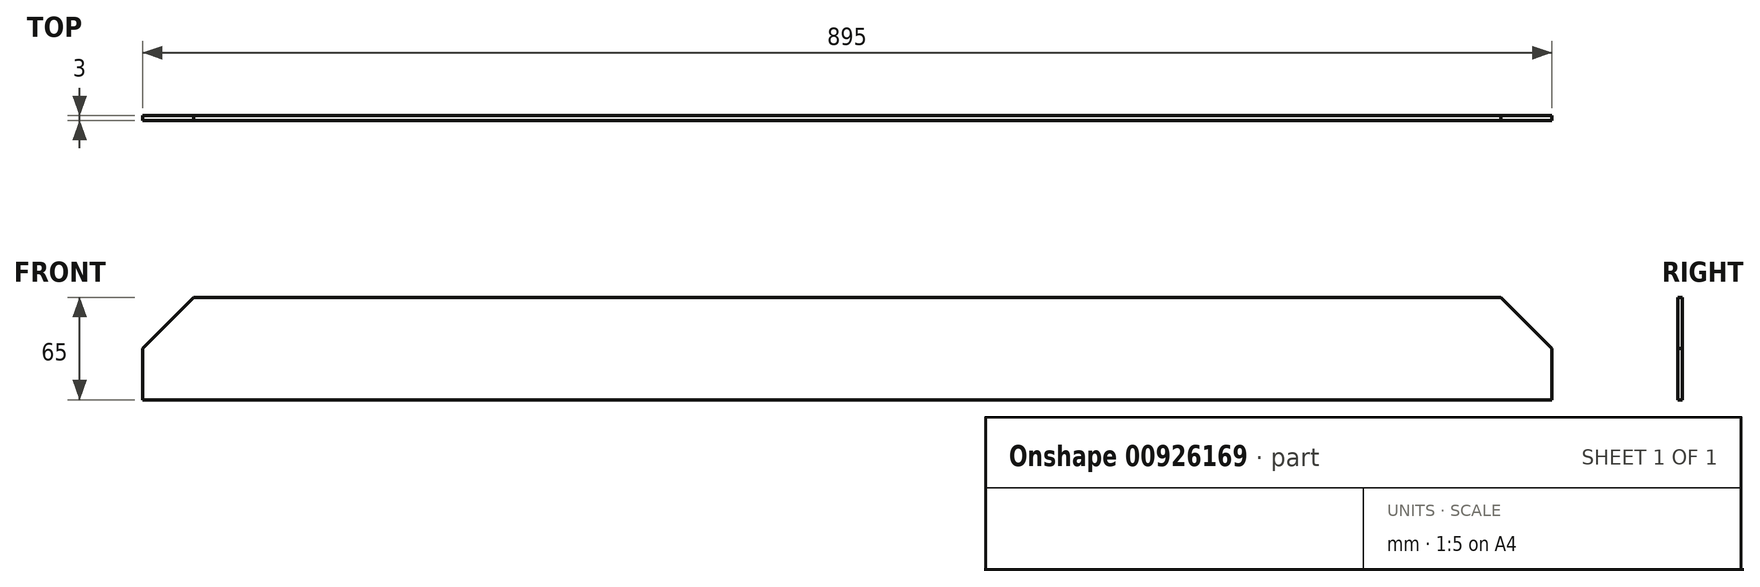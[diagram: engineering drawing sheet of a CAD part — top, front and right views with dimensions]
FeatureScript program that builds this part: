
annotation { "Feature Type Name" : "Feature", "Feature Type Description" : "" }
export const myFeature = defineFeature(function(context is Context, id is Id, definition is map)
    precondition{}
    {
        {
            var Q0;
            Q0=qCreatedBy(makeId("Top.planeOp"),FACE);
            var sketch = newSketch(context, id + "F0", { "sketchPlane" : qUnion([Q0])});
            skLineSegment(sketch, "E0.bottom", {"start": v(0, 0) * mm, "end": v(895, 0) * mm});
            skLineSegment(sketch, "E0.top", {"start": v(0, 3) * mm, "end": v(895, 3) * mm});
            skLineSegment(sketch, "E0.left", {"start": v(0, 0) * mm, "end": v(0, 3) * mm});
            skLineSegment(sketch, "E0.right", {"start": v(895, 0) * mm, "end": v(895, 3) * mm});
            skSolve(sketch);
        }
        {
            var Q0;
            Q0=makeQuery(id+"F0.imprint","IMPRINT",FACE,{"disambiguationData":[TD([[makeQuery(id+"F0.imprint","IMPRINT",EDGE,{"derivedFrom":sQuery(id+"F0.wireOp",EDGE,"E0.bottom")}),1.0]])]});
            extrude(context, id + "F1", {"entities" : qUnion([Q0]), "depth" : 65 * mm, "offsetDistance" : 25 * mm});
        }
        {
            var Q0;
            Q0=makeQuery(id+"F1.opExtrude","SWEPT_FACE",FACE,{"disambiguationData":[OSD([sQuery(id+"F0.wireOp",EDGE,"E0.bottom")])]});
            var sketch = newSketch(context, id + "F2", { "sketchPlane" : qUnion([Q0])});
            skLineSegment(sketch, "E1", {"start": v(0, 32.5) * mm, "end": v(32.5, 65) * mm});
            skLineSegment(sketch, "E2", {"start": v(32.5, 65) * mm, "end": v(0, 65) * mm});
            skLineSegment(sketch, "E3", {"start": v(0, 65) * mm, "end": v(0, 32.5) * mm});
            skLineSegment(sketch, "E4", {"start": v(895, 32.5) * mm, "end": v(862.5, 65) * mm});
            skLineSegment(sketch, "E5", {"start": v(862.5, 65) * mm, "end": v(895, 65) * mm});
            skLineSegment(sketch, "E6", {"start": v(895, 65) * mm, "end": v(895, 32.5) * mm});
            skSolve(sketch);
        }
        {
            var Q0;
            Q0=makeQuery(id+"F2.imprint","IMPRINT",FACE,{"disambiguationData":[TD([[makeQuery(id+"F2.imprint","IMPRINT",EDGE,{"derivedFrom":sQuery(id+"F2.wireOp",EDGE,"E4")}),-1.0]])]});
            var Q1;
            Q1=makeQuery(id+"F2.imprint","IMPRINT",FACE,{"disambiguationData":[TD([[makeQuery(id+"F2.imprint","IMPRINT",EDGE,{"derivedFrom":sQuery(id+"F2.wireOp",EDGE,"E1")}),1.0]])]});
            extrude(context, id + "F3", {"entities" : qUnion([Q0, Q1]), "operationType" : NewBodyOperationType.REMOVE, "endBound" : BoundingType.THROUGH_ALL, "oppositeDirection" : true, "depth" : 25 * mm, "offsetDistance" : 25 * mm});
        }
    });
